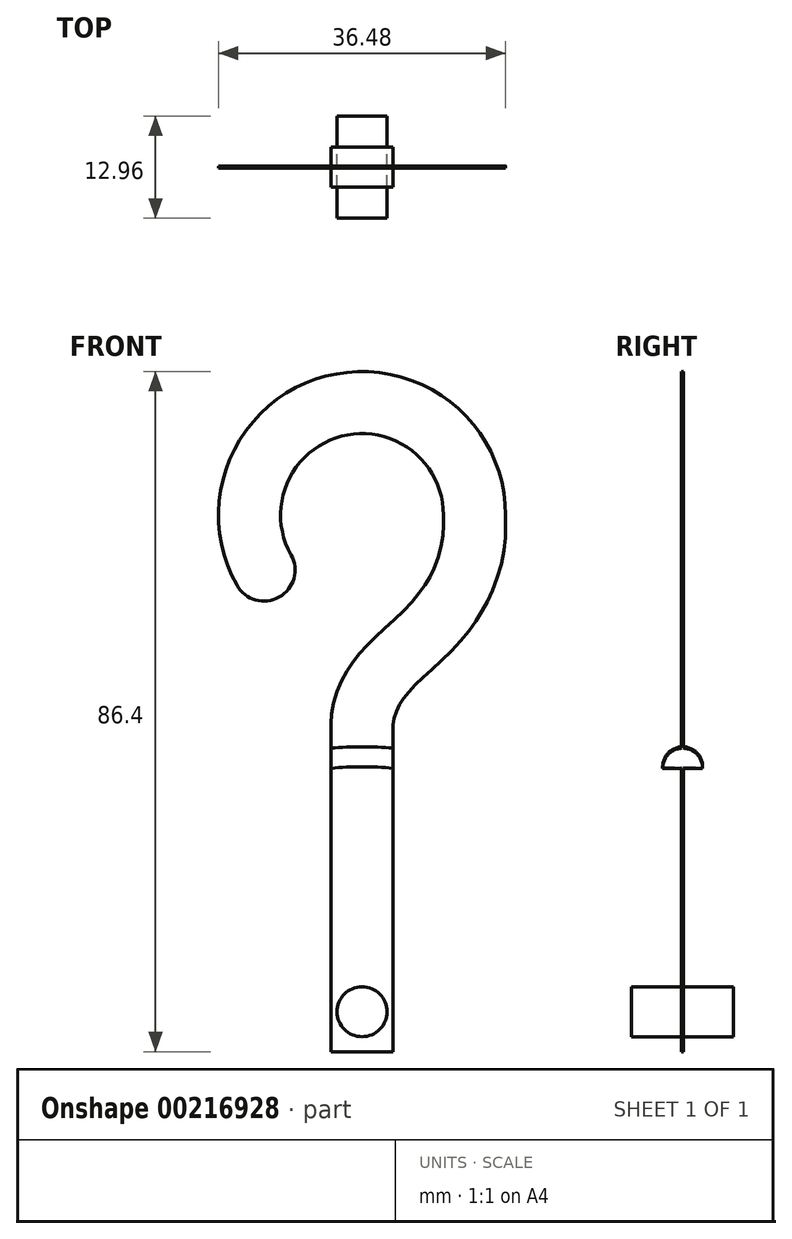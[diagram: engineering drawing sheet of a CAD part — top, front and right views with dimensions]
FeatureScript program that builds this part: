
annotation { "Feature Type Name" : "Feature", "Feature Type Description" : "" }
export const myFeature = defineFeature(function(context is Context, id is Id, definition is map)
    precondition{}
    {
        {
            var Q0;
            Q0=qCreatedBy(makeId("Front.planeOp"),FACE);
            var sketch = newSketch(context, id + "F0", { "sketchPlane" : qUnion([Q0])});
            skCircle(sketch, "E0", {"center": v(0, 0) * mm, "radius": 15.24 * mm});
            skCircle(sketch, "E1", {"center": v(0, 0) * mm, "radius": 15.88 * mm});
            skLineSegment(sketch, "E2", {"start": v(-3.94, 14.72) * mm, "end": v(-3.94, 41.09) * mm});
            skLineSegment(sketch, "E3", {"start": v(-3.94, 14.72) * mm, "end": v(-3.94, 15.38) * mm});
            skLineSegment(sketch, "E4", {"start": v(3.94, 14.72) * mm, "end": v(3.94, 15.38) * mm});
            skLineSegment(sketch, "E5", {"start": v(3.94, 15.38) * mm, "end": v(3.94, 41.09) * mm});
            skArc(sketch, "E6.0", {"start": v(18.23, 68.62) * mm, "mid": v(-4.6, 86.26) * mm, "end": v(-15.9, 59.7) * mm});
            skFitSpline(sketch, "E6.1", {"points": [v(3.94, 41.28) * mm, v(3.94, 41.74) * mm, v(4.02, 42.55) * mm, v(4.3, 43.55) * mm, v(4.72, 44.47) * mm, v(5.35, 45.42) * mm, v(6.2, 46.43) * mm, v(7.6, 47.87) * mm, v(9.81, 49.88) * mm, v(12.31, 52.38) * mm, v(14.23, 54.86) * mm, v(15.56, 57) * mm, v(16.7, 59.43) * mm, v(17.85, 63.08) * mm, v(18.23, 66.27) * mm, v(18.23, 68.62) * mm]});
            skArc(sketch, "E7.0", {"start": v(10.34, 68.62) * mm, "mid": v(-2.61, 78.63) * mm, "end": v(-9.02, 63.56) * mm});
            skFitSpline(sketch, "E7.1", {"points": [v(-3.94, 41.28) * mm, v(-3.94, 42.17) * mm, v(-3.8, 43.9) * mm, v(-3.15, 46.29) * mm, v(-2.16, 48.4) * mm, v(-0.94, 50.21) * mm, v(0.4, 51.78) * mm, v(2.22, 53.64) * mm, v(4.47, 55.69) * mm, v(6.44, 57.68) * mm, v(7.75, 59.38) * mm, v(8.6, 60.75) * mm, v(9.31, 62.28) * mm, v(10.06, 64.62) * mm, v(10.34, 66.84) * mm, v(10.34, 68.62) * mm]});
            skLineSegment(sketch, "E8", {"start": v(-3.94, 41.28) * mm, "end": v(-3.94, 41.09) * mm});
            skLineSegment(sketch, "E9", {"start": v(3.94, 41.28) * mm, "end": v(3.94, 41.09) * mm});
            skArc(sketch, "E10", {"start": v(-9.02, 63.56) * mm, "mid": v(-10.53, 58.2) * mm, "end": v(-15.9, 59.7) * mm});
            skSolve(sketch);
        }
        {
            var Q0;
            Q0=qCreatedBy(makeId("Front.planeOp"),FACE);
            var sketch = newSketch(context, id + "F1", { "sketchPlane" : qUnion([Q0])});
            skArc(sketch, "E11.0", {"start": v(18.23, 76.4) * mm, "mid": v(-4.6, 94.03) * mm, "end": v(-15.9, 67.48) * mm});
            skFitSpline(sketch, "E11.1", {"points": [v(3.94, 49.04) * mm, v(3.94, 49.5) * mm, v(4.02, 50.31) * mm, v(4.3, 51.31) * mm, v(4.72, 52.24) * mm, v(5.35, 53.2) * mm, v(6.2, 54.2) * mm, v(7.6, 55.64) * mm, v(9.81, 57.65) * mm, v(12.31, 60.15) * mm, v(14.23, 62.63) * mm, v(15.56, 64.76) * mm, v(16.7, 67.2) * mm, v(17.85, 70.85) * mm, v(18.23, 74.04) * mm, v(18.23, 76.4) * mm]});
            skArc(sketch, "E12.0", {"start": v(10.34, 76.4) * mm, "mid": v(-2.61, 86.4) * mm, "end": v(-9.02, 71.33) * mm});
            skFitSpline(sketch, "E12.1", {"points": [v(-3.94, 49.04) * mm, v(-3.94, 49.94) * mm, v(-3.8, 51.67) * mm, v(-3.15, 54.05) * mm, v(-2.16, 56.16) * mm, v(-0.94, 57.98) * mm, v(0.4, 59.55) * mm, v(2.22, 61.41) * mm, v(4.47, 63.45) * mm, v(6.44, 65.45) * mm, v(7.75, 67.15) * mm, v(8.6, 68.52) * mm, v(9.31, 70.05) * mm, v(10.06, 72.39) * mm, v(10.34, 74.61) * mm, v(10.34, 76.4) * mm]});
            skLineSegment(sketch, "E13", {"start": v(-3.94, 49.04) * mm, "end": v(-3.94, 48.86) * mm});
            skLineSegment(sketch, "E14", {"start": v(3.94, 49.04) * mm, "end": v(3.94, 48.86) * mm});
            skArc(sketch, "E15", {"start": v(-9.02, 71.33) * mm, "mid": v(-10.53, 65.96) * mm, "end": v(-15.9, 67.48) * mm});
            skLineSegment(sketch, "E16", {"start": v(3.94, 8.22) * mm, "end": v(-3.94, 8.22) * mm});
            skLineSegment(sketch, "E17", {"start": v(3.94, 48.86) * mm, "end": v(3.94, 8.22) * mm});
            skLineSegment(sketch, "E18", {"start": v(-3.94, 48.86) * mm, "end": v(-3.94, 8.22) * mm});
            skCircle(sketch, "E19", {"center": v(0, 13.3) * mm, "radius": 3.18 * mm});
            skCircle(sketch, "E20", {"center": v(0, 3.14) * mm, "radius": 41.28 * mm});
            skCircle(sketch, "E21", {"center": v(0, 3.14) * mm, "radius": 43.82 * mm});
            skSolve(sketch);
        }
        {
            var Q0;
            {var subQ1=sQuery(id+"F1.wireOp",EDGE,"E13");Q0=makeQuery(id+"F1.imprint","IMPRINT",FACE,{"disambiguationData":[TD([[makeQuery(id+"F1.imprint","IMPRINT",EDGE,{"derivedFrom":subQ1}),1.0]])]});}
            var Q1;
            {var subQ5=sQuery(id+"F1.wireOp",EDGE,"E11.0");Q1=makeQuery(id+"F1.imprint","IMPRINT",FACE,{"disambiguationData":[TD([[makeQuery(id+"F1.imprint","IMPRINT",EDGE,{"derivedFrom":subQ5}),1.0]])]});}
            var Q2;
            {var subQ0=sQuery(id+"F1.wireOp",EDGE,"E21");var subQ1=sQuery(id+"F1.wireOp",EDGE,"E11.1");var subQ2=makeQuery(id+"F1.imprint","INTERSECT",VERTEX,{"derivedFrom":[subQ1,subQ0]});Q2=makeQuery(id+"F1.imprint","IMPRINT",FACE,{"disambiguationData":[TD([[makeQuery(id+"F1.imprint","IMPRINT",EDGE,{"disambiguationData":[TD([[subQ2,1.0]])],"derivedFrom":subQ1}),1.0]])]});}
            var Q3;
            {var subQ0=sQuery(id+"F1.wireOp",EDGE,"E21");var subQ1=sQuery(id+"F1.wireOp",EDGE,"E17");var subQ2=makeQuery(id+"F1.imprint","INTERSECT",VERTEX,{"derivedFrom":[subQ1,subQ0]});Q3=makeQuery(id+"F1.imprint","IMPRINT",FACE,{"disambiguationData":[TD([[makeQuery(id+"F1.imprint","IMPRINT",EDGE,{"disambiguationData":[TD([[subQ2,-1.0]])],"derivedFrom":subQ1}),-1.0]])]});}
            var Q4;
            {var subQ1=sQuery(id+"F1.wireOp",EDGE,"E16");Q4=makeQuery(id+"F1.imprint","IMPRINT",FACE,{"disambiguationData":[TD([[makeQuery(id+"F1.imprint","IMPRINT",EDGE,{"derivedFrom":subQ1}),-1.0]])]});}
            extrude(context, id + "F2", {"entities" : qUnion([Q0, Q1, Q2, Q3, Q4]), "endBound" : BoundingType.SYMMETRIC, "depth" : 0.25 * mm});
        }
        {
            var Q0;
            Q0=makeQuery(id+"F1.imprint","IMPRINT",FACE,{"disambiguationData":[TD([[makeQuery(id+"F1.imprint","IMPRINT",EDGE,{"derivedFrom":sQuery(id+"F1.wireOp",EDGE,"E19")}),1.0]])]});
            extrude(context, id + "F3", {"entities" : qUnion([Q0]), "operationType" : NewBodyOperationType.ADD, "endBound" : BoundingType.SYMMETRIC, "depth" : 12.95 * mm});
        }
        {
            var Q0;
            {var subQ0=sQuery(id+"F1.wireOp",EDGE,"E21");var subQ1=sQuery(id+"F1.wireOp",EDGE,"E17");var subQ2=makeQuery(id+"F1.imprint","INTERSECT",VERTEX,{"derivedFrom":[subQ1,subQ0]});Q0=makeQuery(id+"F1.imprint","IMPRINT",FACE,{"disambiguationData":[TD([[makeQuery(id+"F1.imprint","IMPRINT",EDGE,{"disambiguationData":[TD([[subQ2,-1.0]])],"derivedFrom":subQ1}),-1.0]])]});}
            extrude(context, id + "F4", {"entities" : qUnion([Q0]), "operationType" : NewBodyOperationType.ADD, "endBound" : BoundingType.SYMMETRIC, "depth" : 5.08 * mm});
        }
        {
            var Q0;
            Q0=makeQuery(id+"F4.opExtrude","CAP_EDGE",EDGE,{"disambiguationData":[OSD([sQuery(id+"F1.wireOp",EDGE,"E21")])],"isStart":true});
            fillet(context, id + "F5", {"entities" : qUnion([Q0]), "radius" : 2.54 * mm, "tangentPropagation" : true, "allowEdgeOverflow" : false});
        }
        {
            var Q0;
            Q0=makeQuery(id+"F4.opExtrude","CAP_EDGE",EDGE,{"disambiguationData":[OSD([sQuery(id+"F1.wireOp",EDGE,"E21")])],"isStart":false});
            fillet(context, id + "F6", {"entities" : qUnion([Q0]), "radius" : 2.54 * mm, "tangentPropagation" : true, "allowEdgeOverflow" : false});
        }
    });
